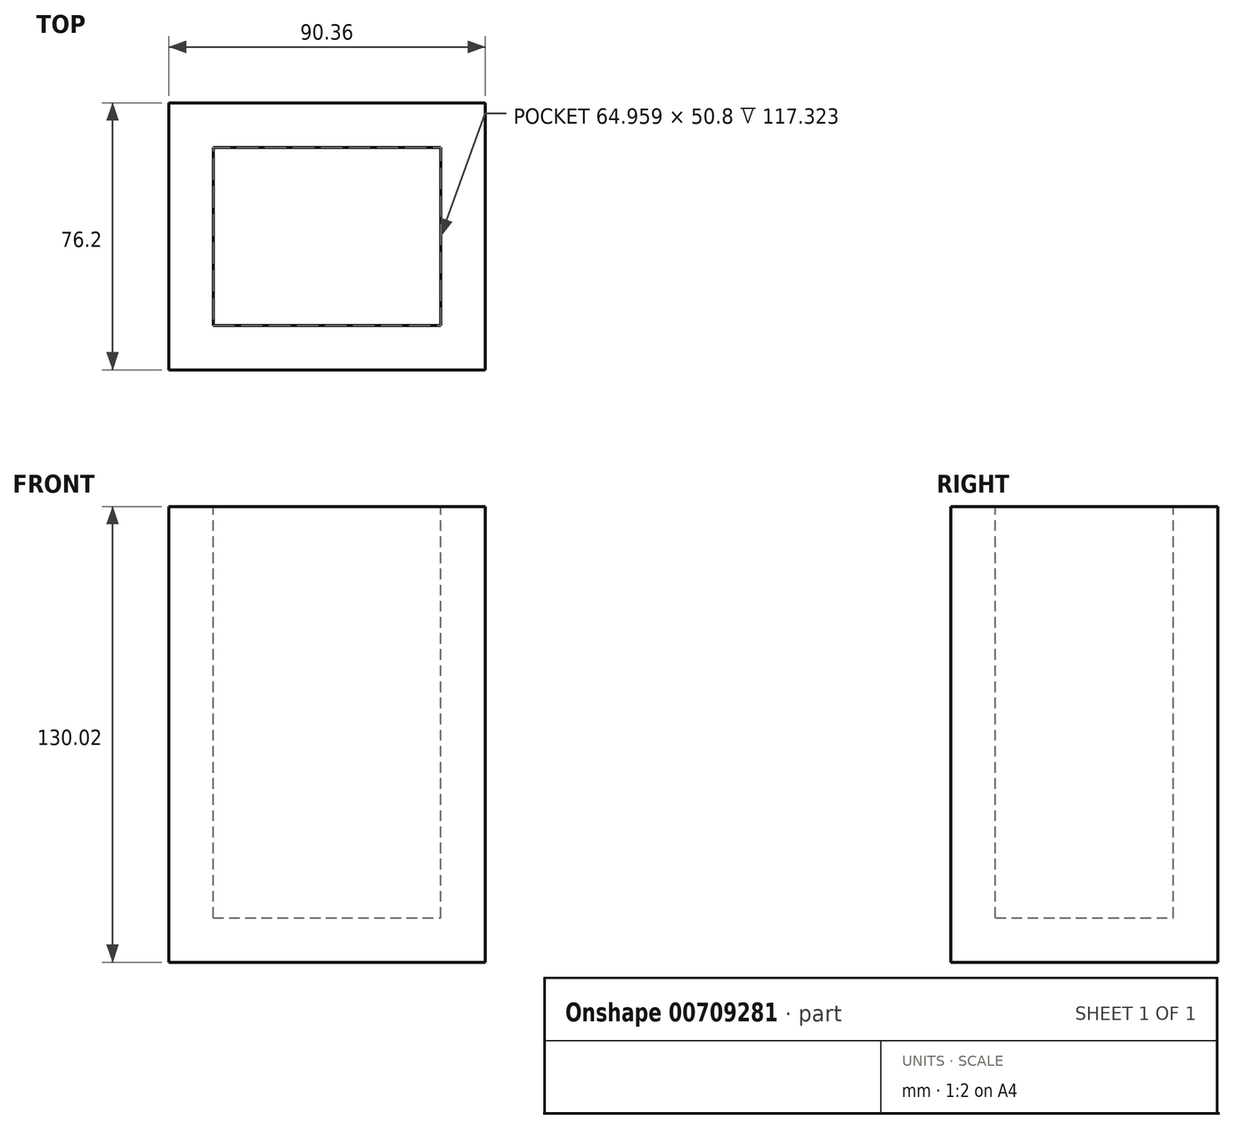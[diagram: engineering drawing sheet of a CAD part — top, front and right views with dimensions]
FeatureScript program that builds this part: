
annotation { "Feature Type Name" : "Feature", "Feature Type Description" : "" }
export const myFeature = defineFeature(function(context is Context, id is Id, definition is map)
    precondition{}
    {
        {
            var Q0;
            Q0=qCreatedBy(makeId("Front.planeOp"),FACE);
            var sketch = newSketch(context, id + "F0", { "sketchPlane" : qUnion([Q0])});
            skLineSegment(sketch, "E0.bottom", {"start": v(-45.18, -65.01) * mm, "end": v(45.18, -65.01) * mm});
            skLineSegment(sketch, "E0.top", {"start": v(-45.18, 65.01) * mm, "end": v(45.18, 65.01) * mm});
            skLineSegment(sketch, "E0.left", {"start": v(-45.18, -65.01) * mm, "end": v(-45.18, 65.01) * mm});
            skLineSegment(sketch, "E0.right", {"start": v(45.18, -65.01) * mm, "end": v(45.18, 65.01) * mm});
            skPoint(sketch, "E0.middle", {"position": v(0, 0) * mm});
            skSolve(sketch);
        }
        {
            var Q0;
            Q0 = qSketchRegion(id + "F0", true);
            extrude(context, id + "F1", {"entities" : qUnion([Q0]), "depth" : 76.2 * mm, "offsetDistance" : 25.4 * mm});
        }
        {
            var Q0;
            Q0=makeQuery(id+"F1.opExtrude","SWEPT_FACE",FACE,{"disambiguationData":[OSD([sQuery(id+"F0.wireOp",EDGE,"E0.top")])]});
            shell(context, id + "F2", {"entities" : qUnion([Q0]), "thickness" : 12.7 * mm});
        }
    });
